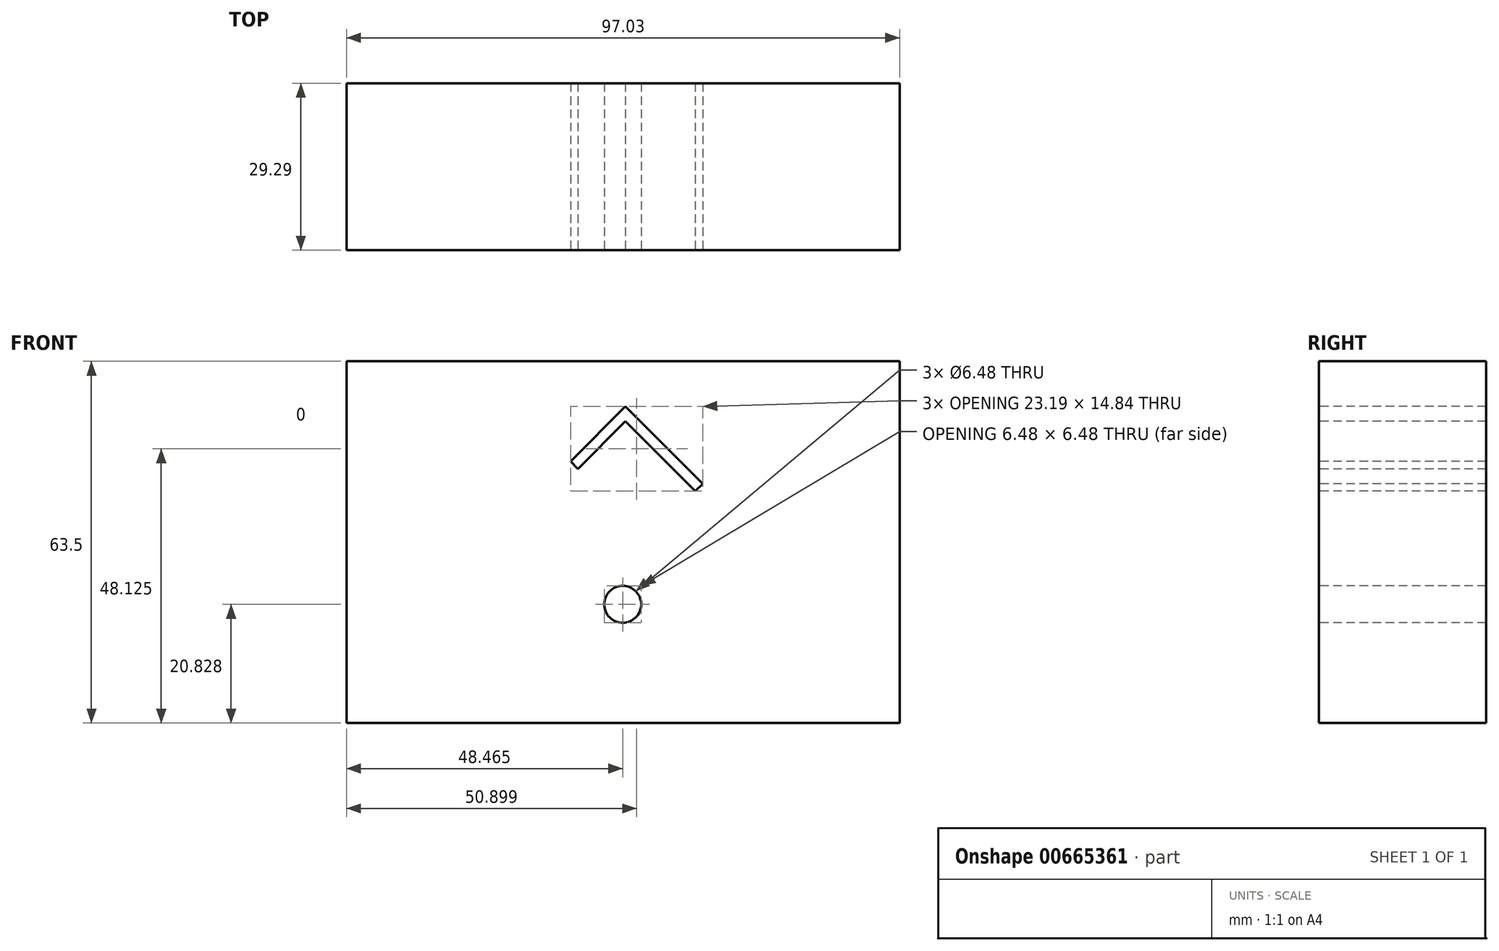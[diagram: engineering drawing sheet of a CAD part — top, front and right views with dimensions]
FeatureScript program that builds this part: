
annotation { "Feature Type Name" : "Feature", "Feature Type Description" : "" }
export const myFeature = defineFeature(function(context is Context, id is Id, definition is map)
    precondition{}
    {
        {
            var Q0;
            Q0=qCreatedBy(makeId("Top.planeOp"),FACE);
            var sketch = newSketch(context, id + "F0", { "sketchPlane" : qUnion([Q0])});
            skLineSegment(sketch, "E0.bottom", {"start": v(-45.16, 14.5) * mm, "end": v(51.87, 14.5) * mm});
            skLineSegment(sketch, "E0.top", {"start": v(-45.16, -14.78) * mm, "end": v(51.87, -14.78) * mm});
            skLineSegment(sketch, "E0.left", {"start": v(-45.16, 14.5) * mm, "end": v(-45.16, -14.78) * mm});
            skLineSegment(sketch, "E0.right", {"start": v(51.87, 14.5) * mm, "end": v(51.87, -14.78) * mm});
            skSolve(sketch);
        }
        {
            var Q0;
            Q0=qSketchRegion(id+"F0",true);
            extrude(context, id + "F1", {"entities" : qUnion([Q0]), "depth" : 63.5 * mm, "offsetDistance" : 25.4 * mm});
        }
        {
            var Q0;
            Q0=makeQuery(id+"F1.opExtrude","SWEPT_FACE",FACE,{"disambiguationData":[OSD([sQuery(id+"F0.wireOp",EDGE,"E0.top")])]});
            var sketch = newSketch(context, id + "F2", { "sketchPlane" : qUnion([Q0])});
            skCircle(sketch, "E1", {"center": v(3.3, 20.83) * mm, "radius": 3.24 * mm});
            skSolve(sketch);
        }
        {
            var Q0;
            Q0=qSketchRegion(id+"F2",true);
            extrude(context, id + "F3", {"entities" : qUnion([Q0]), "operationType" : NewBodyOperationType.REMOVE, "oppositeDirection" : true, "depth" : 50.8 * mm, "offsetDistance" : 25.4 * mm});
        }
        {
            var Q0;
            Q0=makeQuery(id+"F1.opExtrude","SWEPT_FACE",FACE,{"disambiguationData":[OSD([sQuery(id+"F0.wireOp",EDGE,"E0.top")])]});
            var sketch = newSketch(context, id + "F4", { "sketchPlane" : qUnion([Q0])});
            skLineSegment(sketch, "E2", {"start": v(3.8, 55.54) * mm, "end": v(17.33, 42) * mm});
            skLineSegment(sketch, "E3", {"start": v(17.33, 42) * mm, "end": v(16.04, 40.7) * mm});
            skLineSegment(sketch, "E4", {"start": v(-5.85, 45.9) * mm, "end": v(-4.56, 44.6) * mm});
            skLineSegment(sketch, "E5", {"start": v(-4.56, 44.6) * mm, "end": v(3.8, 52.96) * mm});
            skLineSegment(sketch, "E6", {"start": v(3.8, 55.54) * mm, "end": v(-5.85, 45.9) * mm});
            skLineSegment(sketch, "E7", {"start": v(3.8, 52.96) * mm, "end": v(16.04, 40.7) * mm});
            skSolve(sketch);
        }
        {
            var Q0;
            Q0=qSketchRegion(id+"F4",true);
            extrude(context, id + "F5", {"entities" : qUnion([Q0]), "operationType" : NewBodyOperationType.REMOVE, "oppositeDirection" : true, "depth" : 50.8 * mm, "offsetDistance" : 25.4 * mm});
        }
    });
